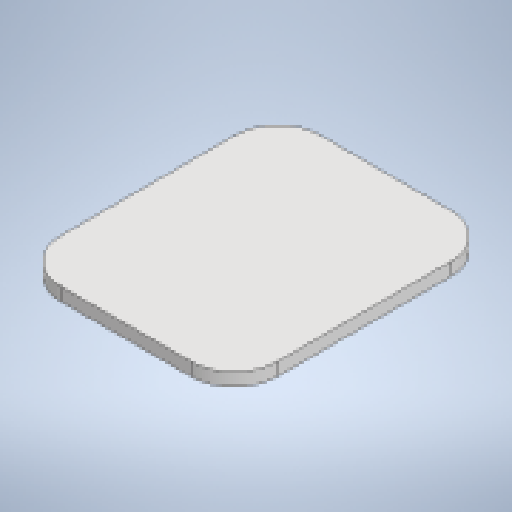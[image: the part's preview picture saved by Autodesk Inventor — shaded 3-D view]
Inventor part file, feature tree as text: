
AUTODESK INVENTOR PART (.ipt)
format: ipt  version: 2025.4 (Build 294407000, 407)  size: 172,032 bytes
history: native  units: mm
features: sheet_metal_op x2, sketch x2, other x2, chamfer x1
ambient origin geometry x8: Origin, YZ Plane, XZ Plane, XY Plane, X Axis, Y Axis, Z Axis, Center Point
bodies: Solid1 (feature_tree)
feature tree (7):
  sheet_metal_op  "Face1"
  chamfer  "Corner Round1"
  sheet_metal_op  "Fold1"
  sketch  "Sketch1"  dims[d0=100.0mm]
  other  "Plate1"
  sketch  "Sketch5"  dims[d1=110.0mm d2=6.0mm d22=20.0mm d23=30.0mm d24=6.0mm d25=3.0mm d26=12.0mm d27=5.0mm d28=30.0deg d29=5.0mm]
  other  "Definition1"
